# Revit family: Somati-System_OGS_Fire-sectional-door_Standard-900mm_EI60
name_source: partatom
category: Doors
revit_build: Autodesk Revit 2018 (Build: 20181011_1500(x64)
units: mm (PartAtom-declared; Revit-internal decimal feet)

## family parameters
Always vertical = Yes
Cut with Voids When Loaded = No
Host = Wall
OmniClass Number = 23.30.10.00
OmniClass Title = Doors
Room Calculation Point = No
Shared = No

## types (1)
- EI 60
    Available surface fnish = Galvanized, powder coating of whole RAL pallet
    BIMobject category = Fire Doors & Shutters
    BIMobject category code = doors-fire
    BIMobject main category = Doors
    BIMobject main category code = doors
    Design country = Poland
    Edition number = 1
    Engine Material = Somati - Stainless Steel
    Fill material = Somati - Insulation
    Fire resistance = EI 60
    Function = Interior
    Gate Control type = SI engine
    Height = 2000 mm  [stored 6.56168 ft]
    Manufacturer = Somati System
    Manufacturer country = Poland
    Manufacturer name = Somati System
    Material main = Steel
    Material secondary = Composite
    Max number of opening cycles = 50000
    Model = OGS
    Nominal height = 0 mm  [stored 0 ft]
    Nominal width = 0 mm  [stored 0 ft]
    Power supply of control panel = 1x230V/50HZ/20A
    Product Guid = 451fb5a0-2dc4-4ddd-8505-073bd876c053
    Product SKU = OGS_FIRE_SECTIONAL_DOOR
    Product data url = https://bimobject.com
    Product family = OGS
    Product group = OGS
    Product url = https://somati-system.pl
    QR code = http://bimobject.com
    Wall Closure = By host
    Warning = Warning
    Weight Net (Kg) = 0
    Width = 2750 mm
    Youtube clip = https://www.youtube.com

note: [stored X ft] marks values corroborated as IEEE doubles in the binary element streams (Revit-internal decimal feet)

## geometry (parser evidence)
native form markers: Sweep x28
no freeform markers — native parametric forms only
